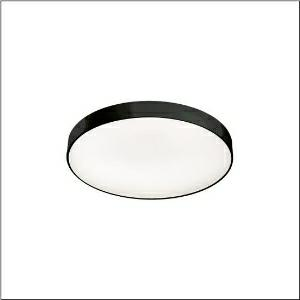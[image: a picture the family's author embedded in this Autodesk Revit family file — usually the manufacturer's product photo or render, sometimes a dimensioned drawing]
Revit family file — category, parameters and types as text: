
# Revit family: round_21_m_51mr36nd0321b
name_source: partatom
category: Lighting Fixtures
units: mm (PartAtom-declared; Revit-internal decimal feet)

## family parameters
Cut with Voids When Loaded = No
Host = Face
Light Source = No
Part Type = Normal
Room Calculation Point = No
Round Connector Dimension = Use Diameter
Shared = No

## types (1)
- Round 21 M (1 x LED, 7170 lm, 54.6 W, 3000K)
    Apparent Load = 55 VA
    CIE Flux Codes = 66 90 98 84 100
    Color Rendering = 80
    Color Temperature = 3000K
    Default Elevation = 1800 mm
    Description = Round 21 M, wall and ceiling luminaire, primary optical cover: micro prismatic cover, of PMMA, transparent, CAT 2 (L<= 3000cd/m²), light emission: direct/indirect distribution, primary light characteristic: symmetric, installation type: surface-mounted, suspended mounting, LED, rated luminous flux: 7.130lm, luminous efficacy: 131lm/W, light colour: 830, colour temperature: 3000K, control gear: DALI 2, with terminal, 5-pole, mains connection: 230V, AC, 50/60Hz, rated input power: 54.6W, housing, of aluminium, coated, black, diameter: 600mm, height: 62mm, protection rating (complete): IP40, insulation class (complete): insulation class I (protective earthing), certification: CE, impact resistance: IK04, permissible operating ambient temperature: -10..+35°C, packaging unit: 1 piece
    Height = 87 mm
    Lamp = 1 x LED
    Lamp Light Flux = 7170 lm
    Lamp Power = 54.6 W
    Lamp count = 1
    Length = 600 mm
    Luminous efficacy = 131 lm/W
    Manufacturer = Siteco
    ModVariant = No
    Model = 51MR36ND0321B
    Mounting Place = Ceiling
    Mounting Type = Surface mounted
    Number of Poles = 1
    OnlyDefault = Yes
    Power Factor = 1
    Product Name = Round 21 M
    Product group = wall and ceiling luminaire
    ProductGroupID = 304
    Protection Class = Protection class I
    Protection Degree = IP 40
    RLX_Detail_Level = 1
    RLX_Emergency_Light_Flux = 0 lm
    RLX_Emergency_Type = 0
    RLX_Emergency_Type_DB = No
    RlxData = <blob elided: 21957 chars, md5=cc502d32>
    Socket = socket
    Standby Power = 0 W
    System Light Flux = 7170 lm
    System Power = 55 W
    Type Comments = Product without accessories
    Type Image = l_1258305.jpg
    URL = http://relux.com
    VarID = ---
    Voltage = 0 V
    Weight = 0.00 kg
    Width = 0 mm  [stored 0 ft]

note: [stored X ft] marks values corroborated as IEEE doubles in the binary element streams (Revit-internal decimal feet)

## geometry (parser evidence)
native form markers: Blend x4, Sweep x14
no freeform markers — native parametric forms only
